FCSTD DOCUMENT  (FreeCAD 1.0R39109 (Git))
Label: YawBearing_Extended_Assembly
License: All rights reserved
LicenseURL: http://en.wikipedia.org/wiki/All_rights_reserved
objects: App::Link×5, App::Part×2, Spreadsheet::Sheet×1
EXTERNAL_REF file=../YawBearing_Pipe.FCStd obj=Tube
EXTERNAL_REF file=YawBearing_Extended_Side.FCStd obj=Body
EXTERNAL_REF file=YawBearing_Extended_Top.FCStd obj=Body
EXTERNAL_REF file=../../Master_of_Puppets.FCStd obj=Alternator
EXTERNAL_REF file=../../Master_of_Puppets.FCStd obj=HighEndStop
EXTERNAL_REF file=../../Master_of_Puppets.FCStd obj=Spreadsheet
EXTERNAL_REF file=../../Master_of_Puppets.FCStd obj=YawBearing
EXTERNAL_REF file=../YawBearing_ArcWireSupport.FCStd obj=PadBody
EXTERNAL_REF file=../YawBearing_SafetyCatch.FCStd obj=Body

FEATURE [App::Link] Link  label="Pipe"
  LinkTransform = true
  LinkedObject = -> <external ../YawBearing_Pipe.FCStd>#Tube
FEATURE [App::Link] Link001  label="Side"
  LinkPlacement = pos=(19.5302,-101.25,-49.9296) rot=(0,1,0;0rad)
  LinkTransform = true
  LinkedObject = -> <external YawBearing_Extended_Side.FCStd>#Body
  Placement = pos=(19.5302,-101.25,-49.9296) rot=(0,1,0;0rad)
  expr: .LinkPlacement.Base.x = Spreadsheet.SideX
  expr: .LinkPlacement.Base.y = Spreadsheet.SideY
  expr: .LinkPlacement.Base.z = Spreadsheet.SideZ
  expr: .LinkPlacement.Rotation.Angle = Spreadsheet.SideYAngle
FEATURE [App::Link] Link002  label="Top"
  LinkPlacement = pos=(-44.45,10,-49.9296) rot=(0,0,1;0rad)
  LinkedObject = -> <external YawBearing_Extended_Top.FCStd>#Body
  Placement = pos=(-44.45,10,-49.9296) rot=(0,0,1;0rad)
  expr: Placement = Spreadsheet.ExtendedTopPlacement
FEATURE [Spreadsheet::Sheet] Spreadsheet
  cells = A1='Inputs; A2='YawPipeDiameter; B2(YawPipeDiameter)==Master_of_Puppets#Spreadsheet.YawPipeDiameter; A3='PipeThickness; B3(PipeThickness)==Master_of_Puppets#Spreadsheet.PipeThickness; A4='FlatMetalThickness; B4(FlatMetalThickness)==Master_of_Puppets#Spreadsheet.FlatMetalThickness; A5='Width; B5(Width)==Master_of_Puppets#YawBearing.MM; A6='RotorDiskRadius; B6(RotorDiskRadius)==Master_of_Puppets#Spreadsheet.RotorDiskRadius; A7='k; B7(k)==Master_of_Puppets#Alternator.k; A8='YawBearingPlateTopHoleRadius; B8(YawBearingPlateTopHoleRadius)==Master_of_Puppets#YawBearing.YawBearingPlateTopHoleRadius; A9='SafetyCatchZ; B9(SafetyCatchZ)==Master_of_Puppets#HighEndStop.SafetyCatchZ; A10='SafetyCatchPartAngle; B10(SafetyCatchPartAngle)==Master_of_Puppets#HighEndStop.SafetyCatchAngle; A11='YawPipeLength; B11(YawPipeLength)==Master_of_Puppets#HighEndStop.YawPipeLength; A12='TopAngle; B12(TopAngle)==Master_of_Puppets#YawBearing.TopAngle; A13='YawPipeRadius; B13(YawPipeRadius)==Master_of_Puppets#YawBearing.YawPipeRadius; A14='HalfWidth; B14(HalfWidth)==Master_of_Puppets#YawBearing.HalfWidth; A15='ArcWireSupportLength; B15(ArcWireSupportLength)==Master_of_Puppets#YawBearing.ArcWireSupportLength; A16='SideYAngle; B16(SideYAngle)==Master_of_Puppets#YawBearing.SideYAngle; A17='ExtendedTopPlacement; B17(ExtendedTopPlacement)==Master_of_Puppets#YawBearing.ExtendedTopPlacement; A18='ArcWireSupport; A19='Offset; B19(Offset)==sqrt((ArcWireSupportLength / 2) ^ 2 / 2); C19='from a^2 + b^2 = c^2; A20='X; B20='Y; C20='Z; A21(ArcWireSupportX)==YawBearingPlateTopHoleRadius * cos(45) + Offset; B21(ArcWireSupportY)==FlatMetalThickness; C21(ArcWireSupportZ)==YawBearingPlateTopHoleRadius * sin(45) + Offset; A22='Side; A23='X; B23='Y; C23='Z; A24(SideX)==Master_of_Puppets#YawBearing.SideX; B24(SideY)==Master_of_Puppets#YawBearing.SideY; C24(SideZ)==Master_of_Puppets#YawBearing.SideZ; A25='SafetyCatch; A26='Rotation; B26='Axis; C26='Angle; A27(SafetyCatchRotation)==create(<<rotation>>; 0; TopAngle; 90); B27(SafetyCatchAxis)==.SafetyCatchRotation.Axis; C27(SafetyCatchAngle)==.SafetyCatchRotation.Angle * 180 / pi; A28='SafetyCatchLinkY; B28(SafetyCatchLinkY)==(YawPipeLength - SafetyCatchZ) * -1
FEATURE [App::Link] Link003  label="ArcWireSupport"
  LinkPlacement = pos=(29.3842,10,29.3842) rot=(0,1,0;2.35619rad)
  LinkedObject = -> <external ../YawBearing_ArcWireSupport.FCStd>#PadBody
  Placement = pos=(29.3842,10,29.3842) rot=(0,1,0;2.35619rad)
  expr: .Placement.Base.x = Spreadsheet.ArcWireSupportX
  expr: .Placement.Base.y = Spreadsheet.ArcWireSupportY
  expr: .Placement.Base.z = Spreadsheet.ArcWireSupportZ
FEATURE [App::Link] Link004  label="SafetyCatch"
  LinkPlacement = pos=(0,-12.1663,0) rot=(0.862856,0.357407,-0.357407;1.71777rad)
  LinkedObject = -> <external ../YawBearing_SafetyCatch.FCStd>#Body
  Placement = pos=(0,-12.1663,0) rot=(0.862856,0.357407,-0.357407;1.71777rad)
  expr: .LinkPlacement.Base.y = Spreadsheet.SafetyCatchLinkY
  expr: .LinkPlacement.Rotation.Angle = Spreadsheet.SafetyCatchAngle
  expr: .LinkPlacement.Rotation.Axis = Spreadsheet.SafetyCatchAxis
  expr: .Placement.Base.y = Spreadsheet.SafetyCatchLinkY
  expr: .Placement.Rotation.Angle = Spreadsheet.SafetyCatchAngle
  expr: .Placement.Rotation.Axis = Spreadsheet.SafetyCatchAxis
FEATURE [App::Part] Part001  label="SafetyCatchPart"
  Group = -> [Link004]
  Origin = -> Origin001
  Placement = pos=(0,0,0) rot=(0,-1,0;0.062891rad)
  expr: .Placement.Rotation.Angle = Spreadsheet.SafetyCatchPartAngle
FEATURE [App::Part] Part  label="YawBearing_Extended_Assembly"
  Group = -> [Link001,Link002,Link,Link003,Part001]
  Origin = -> Origin

RESOLVED EXTERNAL PARTS (link-assembly join: the EXTERNAL_REF files above that resolve inside this repo's crawl, each included once):
---- part ../../Master_of_Puppets.FCStd = doc fcstd_6404554055c4 (61625 chars; too large to inline — full recipe in that document) ----
---- part ../YawBearing_ArcWireSupport.FCStd = doc fcstd_3435764e4c97 ----
FCSTD DOCUMENT  (FreeCAD 0.20R29177 (Git))
Label: YawBearing_ArcWireSupport
License: All rights reserved
LicenseURL: http://en.wikipedia.org/wiki/All_rights_reserved
objects: Sketcher::SketchObject×1, PartDesign::Pad×1, PartDesign::Body×1, Spreadsheet::Sheet×1
note: 4 computed .brp shape members not serialized (recipe doc carries the construction recipe); baked Part::Feature solids carry a one-line shape summary decoded from their .brp
EXTERNAL_REF file=../Master_of_Puppets.FCStd obj=YawBearing

FEATURE [Sketcher::SketchObject] Sketch
  FullyConstrained = true
  MapMode = 5
  Support = -> [XY_Plane001]
  expr: Constraints[8] = Spreadsheet.ArcWireSupportThickness
  expr: Constraints[9] = Spreadsheet.ArcWireSupportLength / 2
  sketch-geometry (4):
    g0: ArcOfCircle CenterX=0 CenterY=0 CenterZ=0 NormalX=0 NormalY=0 NormalZ=1 AngleXU=0 Radius=17.075 StartAngle=-9e-16 EndAngle=3.14159
    g1: ArcOfCircle CenterX=-1e-16 CenterY=0 CenterZ=0 NormalX=0 NormalY=0 NormalZ=1 AngleXU=0 Radius=22.075 StartAngle=-8.9e-15 EndAngle=3.14159
    g2: LineSegment StartX=-22.075 StartY=6.9728e-12 StartZ=0 EndX=-17.075 EndY=-1.268e-13 EndZ=0
    g3: LineSegment StartX=17.075 StartY=-1.52e-14 StartZ=0 EndX=22.075 EndY=-1.961e-13 EndZ=0
  constraints (12):
    c: Coincident(g0,g-1)
    c: PointOnObject(g0,g-1)
    c: PointOnObject(g0,g-1)
    c: Coincident(g1,g-1)
    c: PointOnObject(g1,g-1)
    c: Coincident(g2,g1)
    c: Coincident(g2,g0)
    c: Coincident(g3,g1)
    c: DistanceX(g2,g2) = 5
    c: DistanceX(g-2,g1) = 22.075
    c: Coincident(g0,g3)
    c: PointOnObject(g1,g-1)
FEATURE [PartDesign::Pad] Pad
  AllowMultiFace = false
  Direction = (0,0,1)
  Length = 10
  Length2 = 100
  Midplane = true
  Profile = -> Sketch
  Type = 0
  expr: Length = Spreadsheet.ArcWireSupportWidth
FEATURE [PartDesign::Body] PadBody  label="ArcWireSupport"
  Group = -> [Sketch,Pad]
  Origin = -> Origin001
  Tip = -> Pad
FEATURE [Spreadsheet::Sheet] Spreadsheet
  cells = A1=Inputs; A2=ArcWireSupportThickness; B2(ArcWireSupportThickness)==Master_of_Puppets#YawBearing.ArcWireSupportThickness; A3=ArcWireSupportWidth; B3(ArcWireSupportWidth)==Master_of_Puppets#YawBearing.ArcWireSupportWidth; A4=ArcWireSupportLength; B4(ArcWireSupportLength)==Master_of_Puppets#YawBearing.ArcWireSupportLength
---- part ../YawBearing_SafetyCatch.FCStd = doc fcstd_353e2f168a8f ----
FCSTD DOCUMENT  (FreeCAD 0.21R33675 (Git))
Label: YawBearing_SafetyCatch
License: All rights reserved
LicenseURL: http://en.wikipedia.org/wiki/All_rights_reserved
objects: Sketcher::SketchObject×1, PartDesign::Pad×1, PartDesign::Body×1, Spreadsheet::Sheet×1
note: 4 computed .brp shape members not serialized (recipe doc carries the construction recipe); baked Part::Feature solids carry a one-line shape summary decoded from their .brp
EXTERNAL_REF file=../Master_of_Puppets.FCStd obj=HighEndStop
EXTERNAL_REF file=../Master_of_Puppets.FCStd obj=Spreadsheet

FEATURE [Sketcher::SketchObject] Sketch
  FullyConstrained = true
  MapMode = 5
  Placement = pos=(0,0,0) rot=(0,1,0;3.14159rad)
  Support = -> [XY_Plane]
  expr: Constraints[14] = Spreadsheet.Width
  expr: Constraints[15] = Spreadsheet.Length
  expr: Constraints[1] = Spreadsheet.YawPipeRadius
  sketch-geometry (6):
    g0: LineSegment StartX=156.662 StartY=47.7203 StartZ=0 EndX=156.662 EndY=-47.7203 EndZ=0
    g1: LineSegment StartX=57.15 StartY=-47.7203 StartZ=0 EndX=57.15 EndY=47.7202 EndZ=0
    g2: Circle CenterX=0 CenterY=0 CenterZ=0 NormalX=0 NormalY=0 NormalZ=1 AngleXU=0 Radius=57.15
    g3: LineSegment StartX=156.662 StartY=47.7203 StartZ=0 EndX=31.4468 EndY=47.7203 EndZ=0
    g4: LineSegment StartX=156.662 StartY=-47.7203 StartZ=0 EndX=31.4468 EndY=-47.7203 EndZ=0
    g5: ArcOfCircle CenterX=0 CenterY=0 CenterZ=0 NormalX=0 NormalY=0 NormalZ=1 AngleXU=0 Radius=57.15 StartAngle=5.29505 EndAngle=7.27132
  constraints (17):
    c: Symmetric(g0,g0,g-1)
    c: Radius(g2) = 57.15
    c: Tangent(g2,g1)
    c: PointOnObject(g3,g2)
    c: Horizontal(g3)
    c: Coincident(g5,g2)
    c: Coincident(g5,g3)
    c: Coincident(g5,g4)
    c: Horizontal(g4)
    c: Coincident(g4,g0)
    c: Coincident(g3,g0)
    c: Vertical(g1)
    c: PointOnObject(g1,g3)
    c: PointOnObject(g1,g4)
    c: DistanceY(g0,g0) = 95.4405
    c: DistanceX(g1,g0) = 99.5122
    c: Coincident(g5,g-1)
FEATURE [PartDesign::Pad] Pad
  Direction = (0,0,-1)
  Length = 12
  Length2 = 100
  Profile = -> Sketch
  Type = 0
  expr: Length = Spreadsheet.FlatMetalThickness
FEATURE [PartDesign::Body] Body  label="YawBearing_SafetyCatch"
  Group = -> [Sketch,Pad]
  Openafpm_Flat = true
  Origin = -> Origin
  Tip = -> Pad
FEATURE [Spreadsheet::Sheet] Spreadsheet
  cells = A1='Inputs; A2='FlatMetalThickness; B2(FlatMetalThickness)==Master_of_Puppets#Spreadsheet.FlatMetalThickness; A3='YawPipeDiameter; B3(YawPipeDiameter)==Master_of_Puppets#Spreadsheet.YawPipeDiameter; A4='CalculatedWindTurbineShape; B4(CalculatedWindTurbineShape)==Master_of_Puppets#Spreadsheet.CalculatedWindTurbineShape; A5='Width; B5(Width)==Master_of_Puppets#HighEndStop.SafetyCatchWidth; A6='Length; B6(Length)==Master_of_Puppets#HighEndStop.SafetyCatchLength; A7='Calculated; A8='YawPipeRadius; B8(YawPipeRadius)==YawPipeDiameter / 2; A9='DistanceFromOrigin; B9(DistanceFromOrigin)==CalculatedWindTurbineShape == <<T>> ? 0 : YawPipeRadius
---- part YawBearing_Extended_Side.FCStd = doc fcstd_1bfa72fa80b7 ----
FCSTD DOCUMENT  (FreeCAD 0.21R33771 (Git))
Label: YawBearing_Extended_Side
License: All rights reserved
LicenseURL: http://en.wikipedia.org/wiki/All_rights_reserved
objects: Sketcher::SketchObject×1, PartDesign::Pad×1, PartDesign::Body×1, Spreadsheet::Sheet×1
note: 4 computed .brp shape members not serialized (recipe doc carries the construction recipe); baked Part::Feature solids carry a one-line shape summary decoded from their .brp
EXTERNAL_REF file=../../Master_of_Puppets.FCStd obj=Spreadsheet
EXTERNAL_REF file=../../Master_of_Puppets.FCStd obj=YawBearing

FEATURE [Sketcher::SketchObject] Sketch
  FullyConstrained = true
  MapMode = 5
  Support = -> [XY_Plane]
  expr: Constraints[10] = Spreadsheet.Width / 2
  expr: Constraints[11] = Spreadsheet.X
  expr: Constraints[8] = Spreadsheet.Width
  expr: Constraints[9] = Spreadsheet.SideLength
  sketch-geometry (4):
    g0: LineSegment StartX=-144.55 StartY=-50.625 StartZ=0 EndX=144.55 EndY=-50.625 EndZ=0
    g1: LineSegment StartX=144.55 StartY=-50.625 StartZ=0 EndX=144.55 EndY=50.625 EndZ=0
    g2: LineSegment StartX=144.55 StartY=50.625 StartZ=0 EndX=-144.55 EndY=50.625 EndZ=0
    g3: LineSegment StartX=-144.55 StartY=50.625 StartZ=0 EndX=-144.55 EndY=-50.625 EndZ=0
  constraints (12):
    c: Coincident(g0,g1)
    c: Coincident(g1,g2)
    c: Coincident(g2,g3)
    c: Coincident(g3,g0)
    c: Horizontal(g0)
    c: Horizontal(g2)
    c: Vertical(g1)
    c: Vertical(g3)
    c: DistanceY(g1,g1) = 101.25
    c: DistanceX(g2,g2) = 289.1
    c: DistanceY(g-1,g2) = 50.625
    c: Distance(g-1,g1) = 144.55
FEATURE [PartDesign::Pad] Pad
  AllowMultiFace = false
  Direction = (0,0,1)
  Length = 10
  Length2 = 100
  Profile = -> Sketch
  Type = 0
  expr: Length = Spreadsheet.FlatMetalThickness
FEATURE [PartDesign::Body] Body  label="YawBearing_Extended_Side"
  Group = -> [Sketch,Pad]
  Openafpm_Flat = true
  Origin = -> Origin
  Placement = pos=(144.55,50.625,0) rot=(0,0,1;0rad)
  Tip = -> Pad
  expr: .Placement.Base.x = Spreadsheet.X
  expr: .Placement.Base.y = Spreadsheet.Y
  expr: .Placement.Base.z = Spreadsheet.Z
FEATURE [Spreadsheet::Sheet] Spreadsheet
  cells = A1='Inputs; A2='FlatMetalThickness; B2(FlatMetalThickness)==Master_of_Puppets#Spreadsheet.FlatMetalThickness; A3='Width; B3(Width)==Master_of_Puppets#YawBearing.SideWidth; A4='SideLength; B4(SideLength)==Master_of_Puppets#YawBearing.SideLength; A5='Placement; A6='X; B6='Y; C6='Z; A7(X)==SideLength / 2; B7(Y)==Width / 2; C7(Z)=0
---- part YawBearing_Extended_Top.FCStd = doc fcstd_74702fa66131 ----
FCSTD DOCUMENT  (FreeCAD 0.21R33771 (Git))
Label: YawBearing_Extended_Top
License: All rights reserved
LicenseURL: http://en.wikipedia.org/wiki/All_rights_reserved
objects: Sketcher::SketchObject×1, PartDesign::Pad×1, PartDesign::Body×1, Spreadsheet::Sheet×1
note: 4 computed .brp shape members not serialized (recipe doc carries the construction recipe); baked Part::Feature solids carry a one-line shape summary decoded from their .brp
EXTERNAL_REF file=../../Master_of_Puppets.FCStd obj=Spreadsheet
EXTERNAL_REF file=../../Master_of_Puppets.FCStd obj=YawBearing

FEATURE [Sketcher::SketchObject] Sketch
  FullyConstrained = true
  MapMode = 5
  Placement = pos=(0,0,0) rot=(1,0,0;1.5708rad)
  Support = -> [XZ_Plane]
  expr: Constraints[0] = Spreadsheet.YawPipeRadius
  expr: Constraints[11] = Spreadsheet.L
  expr: Constraints[12] = Spreadsheet.TopAngle
  expr: Constraints[13] = Spreadsheet.Width / 2
  expr: Constraints[14] = Spreadsheet.Width
  expr: Constraints[15] = Spreadsheet.YawPipeRadius
  expr: Constraints[2] = Spreadsheet.YawBearingPlateTopHoleRadius
  sketch-geometry (6):
    g0: Circle CenterX=44.45 CenterY=49.9296 CenterZ=0 NormalX=0 NormalY=0 NormalZ=1 AngleXU=0 Radius=44.45
    g1: LineSegment StartX=333.067 StartY=0 StartZ=0 EndX=432.927 EndY=99.8592 EndZ=0
    g2: Circle CenterX=44.45 CenterY=49.9296 CenterZ=0 NormalX=0 NormalY=0 NormalZ=1 AngleXU=0 Radius=17.5
    g3: LineSegment StartX=0 StartY=0 StartZ=0 EndX=333.067 EndY=0 EndZ=0
    g4: LineSegment StartX=432.927 StartY=99.8592 StartZ=0 EndX=0 EndY=99.8592 EndZ=0
    g5: LineSegment StartX=0 StartY=0 StartZ=0 EndX=0 EndY=99.8592 EndZ=0
  constraints (16):
    c: Radius(g0) = 44.45
    c: Coincident(g2,g0)
    c: Radius(g2) = 17.5
    c: Coincident(g3,g-1)
    c: Coincident(g3,g1)
    c: Horizontal(g3)
    c: Coincident(g4,g1)
    c: Horizontal(g4)
    c: Coincident(g5,g3)
    c: Coincident(g5,g4)
    c: Vertical(g5)
    c: DistanceX(g4,g1) = 432.927
    c: Angle(g4,g1) = 0.785398
    c: DistanceY(g3,g2) = 49.9296
    c: DistanceY(g4) = 99.8592
    c: DistanceX(g-2,g2) = 44.45
FEATURE [PartDesign::Pad] Pad
  AllowMultiFace = false
  Direction = (0,-1,-1.035e-13)
  Length = 10
  Length2 = 100
  Placement = pos=(0,0,0) rot=(1,0,0;1.5708rad)
  Profile = -> Sketch
  Type = 0
  expr: Length = Spreadsheet.FlatMetalThickness
FEATURE [PartDesign::Body] Body  label="YawBearing_Extended_Top"
  Group = -> [Sketch,Pad]
  Openafpm_Flat = true
  Origin = -> Origin
  Tip = -> Pad
FEATURE [Spreadsheet::Sheet] Spreadsheet
  cells = A1='Inputs; A2='RotorDiskRadius; B2(RotorDiskRadius)==Master_of_Puppets#Spreadsheet.RotorDiskRadius; A3='YawPipeDiameter; B3(YawPipeDiameter)==Master_of_Puppets#Spreadsheet.YawPipeDiameter; A4='FlatMetalThickness; B4(FlatMetalThickness)==Master_of_Puppets#Spreadsheet.FlatMetalThickness; A5='Width; B5(Width)==Master_of_Puppets#YawBearing.MM; A6='Offset; B6(Offset)==Master_of_Puppets#Spreadsheet.Offset; A7='YawBearingPlateTopHoleRadius; B7(YawBearingPlateTopHoleRadius)==Master_of_Puppets#YawBearing.YawBearingPlateTopHoleRadius; A8='TopAngle; B8(TopAngle)==Master_of_Puppets#YawBearing.TopAngle; A9='L; B9(L)==Master_of_Puppets#YawBearing.L; A10='Calculated; A11='YawPipeRadius; B11(YawPipeRadius)==YawPipeDiameter / 2
